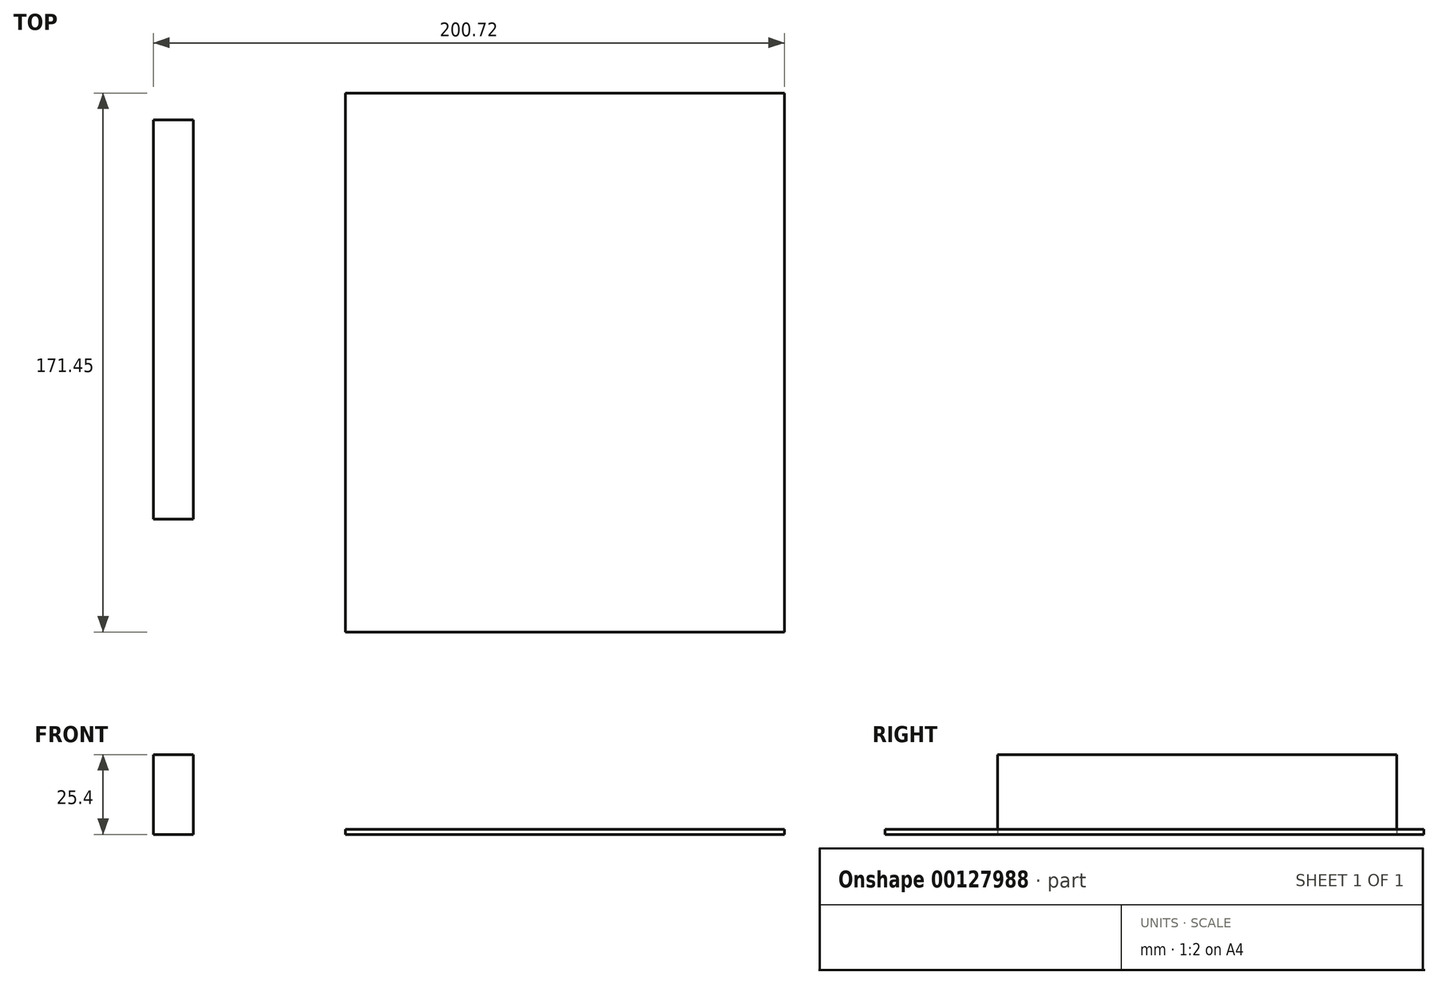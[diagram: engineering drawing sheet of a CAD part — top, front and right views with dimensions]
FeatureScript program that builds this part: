
annotation { "Feature Type Name" : "Feature", "Feature Type Description" : "" }
export const myFeature = defineFeature(function(context is Context, id is Id, definition is map)
    precondition{}
    {
        {
            var Q0;
            Q0=qCreatedBy(makeId("Top.planeOp"),FACE);
            var sketch = newSketch(context, id + "F0", { "sketchPlane" : qUnion([Q0])});
            skLineSegment(sketch, "E0.bottom", {"start": v(-82.33, 83.44) * mm, "end": v(57.37, 83.44) * mm});
            skLineSegment(sketch, "E0.top", {"start": v(-82.33, -88) * mm, "end": v(57.37, -88) * mm});
            skLineSegment(sketch, "E0.left", {"start": v(-82.33, 83.44) * mm, "end": v(-82.33, -88) * mm});
            skLineSegment(sketch, "E0.right", {"start": v(57.37, 83.44) * mm, "end": v(57.37, -88) * mm});
            skSolve(sketch);
        }
        {
            var Q0;
            Q0=makeQuery(id+"F0.imprint","IMPRINT",FACE,{"disambiguationData":[TD([[makeQuery(id+"F0.imprint","IMPRINT",EDGE,{"derivedFrom":sQuery(id+"F0.wireOp",EDGE,"E0.bottom")}),-1.0]])]});
            extrude(context, id + "F1", {"entities" : qUnion([Q0]), "depth" : 1.59 * mm});
        }
        {
            var Q0;
            Q0=qCreatedBy(makeId("Top.planeOp"),FACE);
            var sketch = newSketch(context, id + "F2", { "sketchPlane" : qUnion([Q0])});
            skLineSegment(sketch, "E1.bottom", {"start": v(-143.35, 74.87) * mm, "end": v(-130.65, 74.87) * mm});
            skLineSegment(sketch, "E1.top", {"start": v(-143.35, -52.13) * mm, "end": v(-130.65, -52.13) * mm});
            skLineSegment(sketch, "E1.left", {"start": v(-143.35, 74.87) * mm, "end": v(-143.35, -52.13) * mm});
            skLineSegment(sketch, "E1.right", {"start": v(-130.65, 74.87) * mm, "end": v(-130.65, -52.13) * mm});
            skSolve(sketch);
        }
        {
            var Q0;
            Q0 = qSketchRegion(id + "F2", true);
            extrude(context, id + "F3", {"entities" : qUnion([Q0]), "depth" : 25.4 * mm});
        }
    });
